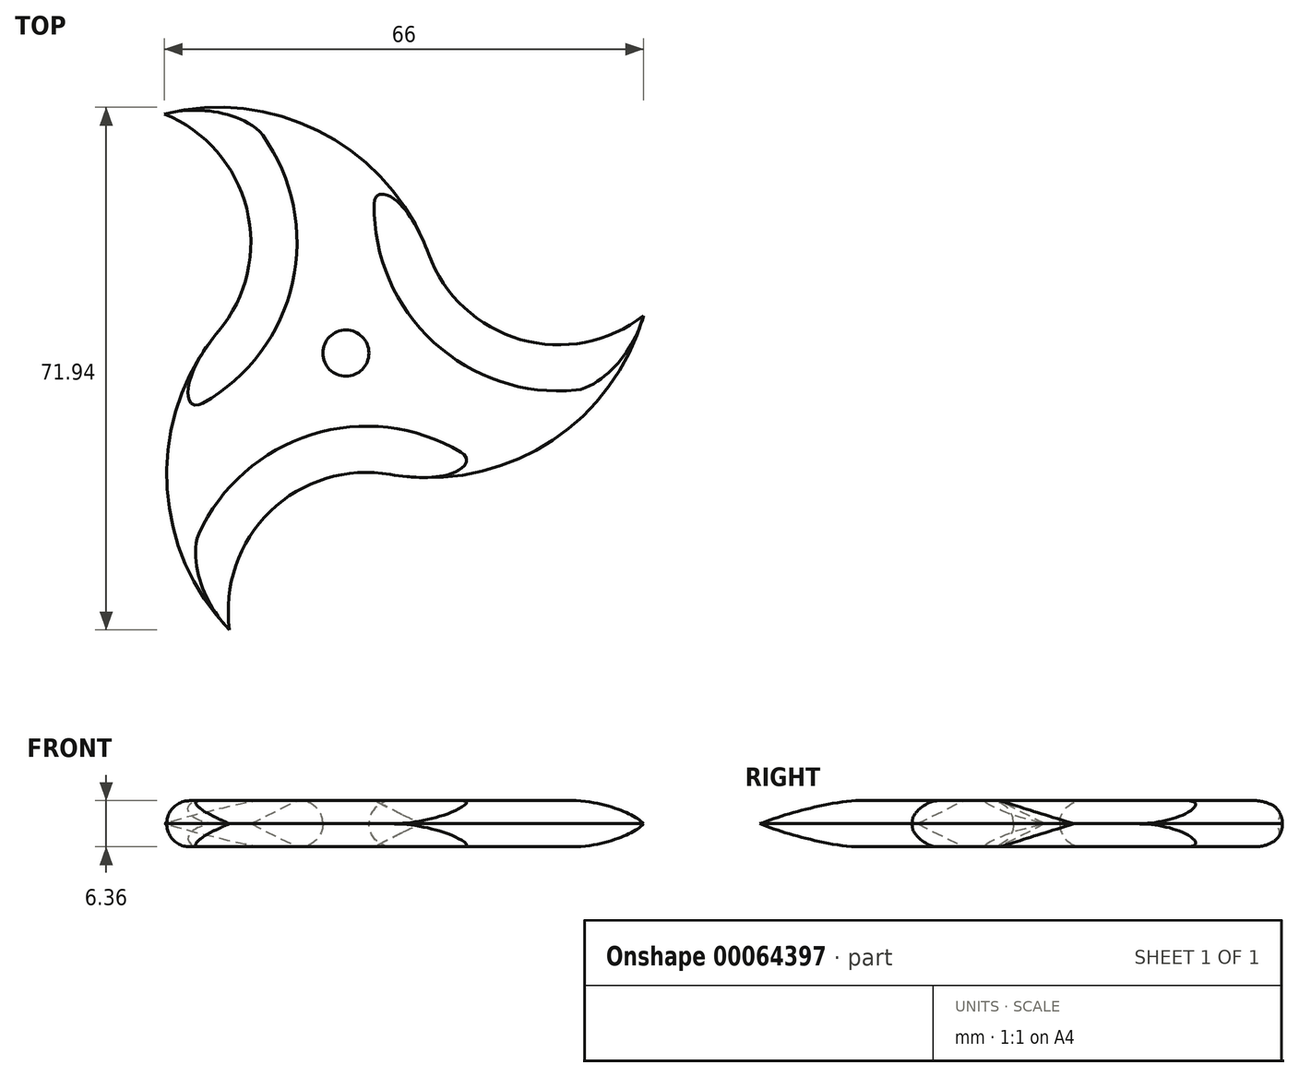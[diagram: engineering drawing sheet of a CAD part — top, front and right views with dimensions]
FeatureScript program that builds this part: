
annotation { "Feature Type Name" : "Feature", "Feature Type Description" : "" }
export const myFeature = defineFeature(function(context is Context, id is Id, definition is map)
    precondition{}
    {
        {
            var Q0;
            Q0=qCreatedBy(makeId("Top.planeOp"),FACE);
            var sketch = newSketch(context, id + "F0", { "sketchPlane" : qUnion([Q0])});
            skCircle(sketch, "E0.cCircle", {"center": v(0, 0) * mm, "radius": 17.78 * mm, "construction": true});
            skLineSegment(sketch, "E0.0", {"start": v(-17.52, 3.05) * mm, "end": v(11.4, 13.65) * mm});
            skLineSegment(sketch, "E0.1", {"start": v(11.4, 13.65) * mm, "end": v(6.12, -16.7) * mm});
            skLineSegment(sketch, "E0.2", {"start": v(6.12, -16.7) * mm, "end": v(-17.52, 3.05) * mm});
            skCircle(sketch, "E1", {"center": v(0, 0) * mm, "radius": 3.18 * mm});
            skArc(sketch, "E2", {"start": v(-17.52, 3.05) * mm, "mid": v(-24.66, -17.81) * mm, "end": v(-16.02, -38.1) * mm});
            skArc(sketch, "E3", {"start": v(6.12, -16.7) * mm, "mid": v(-10.4, -21.77) * mm, "end": v(-16.02, -38.1) * mm});
            skArc(sketch, "E4.1.0", {"start": v(11.4, 13.65) * mm, "mid": v(24.05, 1.88) * mm, "end": v(41, 5.18) * mm});
            skArc(sketch, "E4.1.1", {"start": v(6.12, -16.7) * mm, "mid": v(27.75, -12.45) * mm, "end": v(41, 5.18) * mm});
            skArc(sketch, "E4.2.0", {"start": v(-17.52, 3.05) * mm, "mid": v(-13.65, 19.89) * mm, "end": v(-24.99, 32.92) * mm});
            skArc(sketch, "E4.2.1", {"start": v(11.4, 13.65) * mm, "mid": v(-3.1, 30.26) * mm, "end": v(-24.99, 32.92) * mm});
            skSolve(sketch);
        }
        {
            var Q0;
            Q0=makeQuery(id+"F0.imprint","IMPRINT",FACE,{"disambiguationData":[TD([[makeQuery(id+"F0.imprint","IMPRINT",EDGE,{"derivedFrom":sQuery(id+"F0.wireOp",EDGE,"E0.2")}),1.0]])]});
            var Q1;
            Q1=makeQuery(id+"F0.imprint","IMPRINT",FACE,{"disambiguationData":[TD([[makeQuery(id+"F0.imprint","IMPRINT",EDGE,{"derivedFrom":sQuery(id+"F0.wireOp",EDGE,"E4.1.0")}),-1.0]])]});
            var Q2;
            Q2=makeQuery(id+"F0.imprint","IMPRINT",FACE,{"disambiguationData":[TD([[makeQuery(id+"F0.imprint","IMPRINT",EDGE,{"derivedFrom":sQuery(id+"F0.wireOp",EDGE,"E4.2.0")}),-1.0]])]});
            var Q3;
            Q3=makeQuery(id+"F0.imprint","IMPRINT",FACE,{"disambiguationData":[TD([[makeQuery(id+"F0.imprint","IMPRINT",EDGE,{"derivedFrom":sQuery(id+"F0.wireOp",EDGE,"E0.2")}),-1.0]])]});
            extrude(context, id + "F1", {"entities" : qUnion([Q0, Q1, Q2, Q3]), "depth" : 3.17 * mm});
        }
        {
            var Q0;
            Q0=makeQuery(id+"F1.opExtrude","CAP_EDGE",EDGE,{"disambiguationData":[OSD([sQuery(id+"F0.wireOp",EDGE,"E4.1.0")])],"isStart":false});
            var Q1;
            Q1=makeQuery(id+"F1.opExtrude","CAP_EDGE",EDGE,{"disambiguationData":[OSD([sQuery(id+"F0.wireOp",EDGE,"E4.2.0")])],"isStart":false});
            var Q2;
            Q2=makeQuery(id+"F1.opExtrude","CAP_EDGE",EDGE,{"disambiguationData":[OSD([sQuery(id+"F0.wireOp",EDGE,"E3")])],"isStart":false});
            chamfer(context, id + "F2", {"entities" : qUnion([Q0, Q1, Q2]), "chamferType" : ChamferType.TWO_OFFSETS, "width1" : 3.17 * mm, "oppositeDirection" : false, "width2" : 6.35 * mm});
        }
        {
            var Q0;
            Q0=makeQuery(id+"F1.opExtrude","CAP_EDGE",EDGE,{"disambiguationData":[OSD([sQuery(id+"F0.wireOp",EDGE,"E4.2.1")])],"isStart":false});
            var Q1;
            Q1=makeQuery(id+"F1.opExtrude","CAP_EDGE",EDGE,{"disambiguationData":[OSD([sQuery(id+"F0.wireOp",EDGE,"E4.1.1")])],"isStart":false});
            var Q2;
            Q2=makeQuery(id+"F1.opExtrude","CAP_EDGE",EDGE,{"disambiguationData":[OSD([sQuery(id+"F0.wireOp",EDGE,"E2")])],"isStart":false});
            var Q3;
            Q3=makeQuery(id+"F1.opExtrude","CAP_EDGE",EDGE,{"disambiguationData":[OSD([sQuery(id+"F0.wireOp",EDGE,"E1")])],"isStart":false});
            fillet(context, id + "F3", {"entities" : qUnion([Q0, Q1, Q2, Q3]), "radius" : 3.17 * mm, "tangentPropagation" : true, "allowEdgeOverflow" : false});
        }
        {
            var Q0;
            Q0=makeQuery(id+"F1.opExtrude","SWEPT_BODY",BODY,{"disambiguationData":[OSD([sQuery(id+"F0.wireOp",EDGE,"E1"),sQuery(id+"F0.wireOp",EDGE,"E2"),sQuery(id+"F0.wireOp",EDGE,"E3"),sQuery(id+"F0.wireOp",EDGE,"E4.1.0"),sQuery(id+"F0.wireOp",EDGE,"E4.1.1"),sQuery(id+"F0.wireOp",EDGE,"E4.2.0"),sQuery(id+"F0.wireOp",EDGE,"E4.2.1")])]});
            var Q1;
            Q1=makeQuery(id+"F1.opExtrude","CAP_FACE",FACE,{"disambiguationData":[OSD([sQuery(id+"F0.wireOp",EDGE,"E1"),sQuery(id+"F0.wireOp",EDGE,"E2"),sQuery(id+"F0.wireOp",EDGE,"E3"),sQuery(id+"F0.wireOp",EDGE,"E4.1.0"),sQuery(id+"F0.wireOp",EDGE,"E4.1.1"),sQuery(id+"F0.wireOp",EDGE,"E4.2.0"),sQuery(id+"F0.wireOp",EDGE,"E4.2.1")])],"isStart":true});
            mirror(context, id + "F4", {"entities" : qUnion([Q0]), "mirrorPlane" : qUnion([Q1])});
        }
    });
